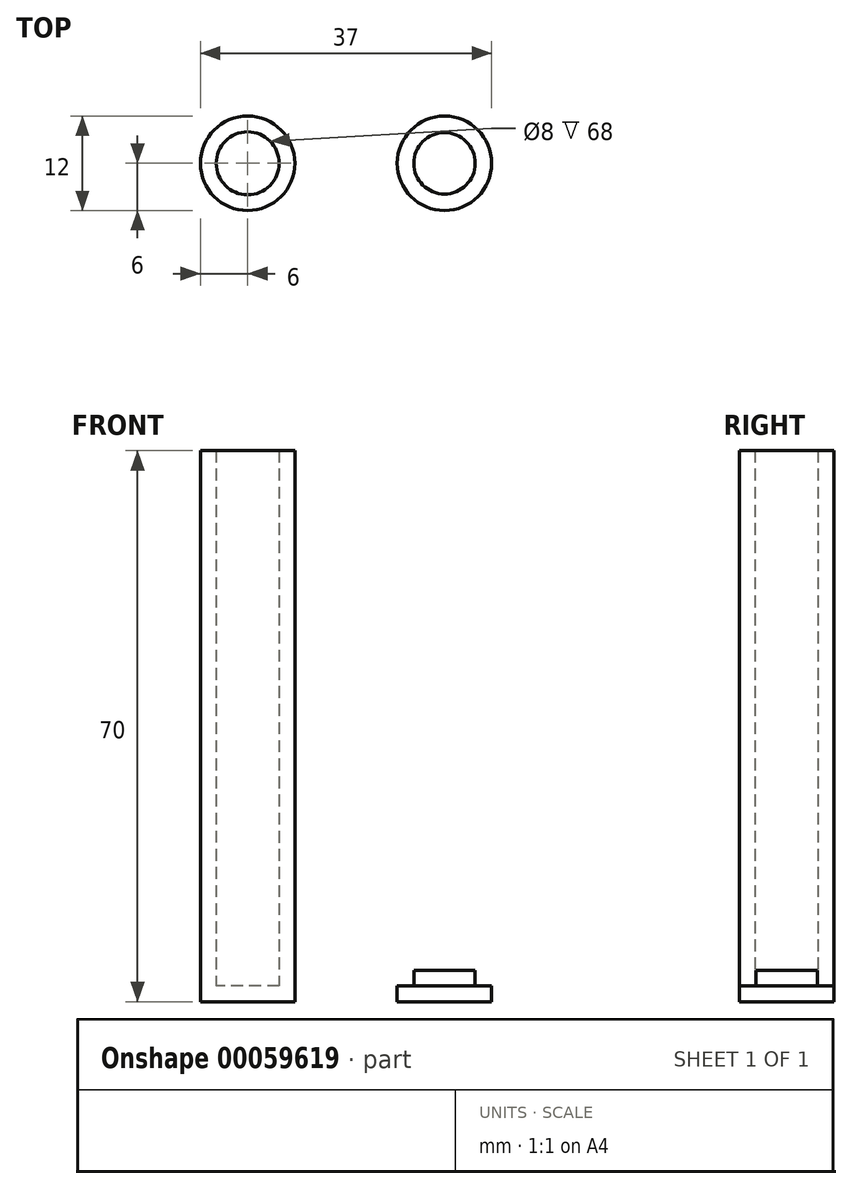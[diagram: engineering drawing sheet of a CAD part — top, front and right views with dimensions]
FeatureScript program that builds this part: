
annotation { "Feature Type Name" : "Feature", "Feature Type Description" : "" }
export const myFeature = defineFeature(function(context is Context, id is Id, definition is map)
    precondition{}
    {
        {
            var Q0;
            Q0=qCreatedBy(makeId("Top.planeOp"),FACE);
            var sketch = newSketch(context, id + "F0", { "sketchPlane" : qUnion([Q0])});
            skCircle(sketch, "E0", {"center": v(0, 0) * mm, "radius": 6 * mm});
            skCircle(sketch, "E1", {"center": v(0, 0) * mm, "radius": 4 * mm});
            skCircle(sketch, "E2", {"center": v(25, 0) * mm, "radius": 6 * mm});
            skCircle(sketch, "E3", {"center": v(25, 0) * mm, "radius": 3.9 * mm});
            skSolve(sketch);
        }
        {
            var Q0;
            Q0=makeQuery(id+"F0.imprint","IMPRINT",FACE,{"disambiguationData":[TD([[makeQuery(id+"F0.imprint","IMPRINT",EDGE,{"derivedFrom":sQuery(id+"F0.wireOp",EDGE,"E0")}),1.0]])]});
            extrude(context, id + "F1", {"entities" : qUnion([Q0]), "depth" : 70 * mm});
        }
        {
            var Q0;
            Q0=makeQuery(id+"F0.imprint","IMPRINT",FACE,{"disambiguationData":[TD([[makeQuery(id+"F0.imprint","IMPRINT",EDGE,{"derivedFrom":sQuery(id+"F0.wireOp",EDGE,"E1")}),1.0]])]});
            extrude(context, id + "F2", {"entities" : qUnion([Q0]), "operationType" : NewBodyOperationType.ADD, "depth" : 2 * mm});
        }
        {
            var Q0;
            Q0=makeQuery(id+"F0.imprint","IMPRINT",FACE,{"disambiguationData":[TD([[makeQuery(id+"F0.imprint","IMPRINT",EDGE,{"derivedFrom":sQuery(id+"F0.wireOp",EDGE,"E2")}),1.0]])]});
            extrude(context, id + "F3", {"entities" : qUnion([Q0]), "depth" : 2 * mm});
        }
        {
            var Q0;
            Q0=makeQuery(id+"F0.imprint","IMPRINT",FACE,{"disambiguationData":[TD([[makeQuery(id+"F0.imprint","IMPRINT",EDGE,{"derivedFrom":sQuery(id+"F0.wireOp",EDGE,"E3")}),1.0]])]});
            extrude(context, id + "F4", {"entities" : qUnion([Q0]), "operationType" : NewBodyOperationType.ADD, "depth" : 4 * mm});
        }
    });
